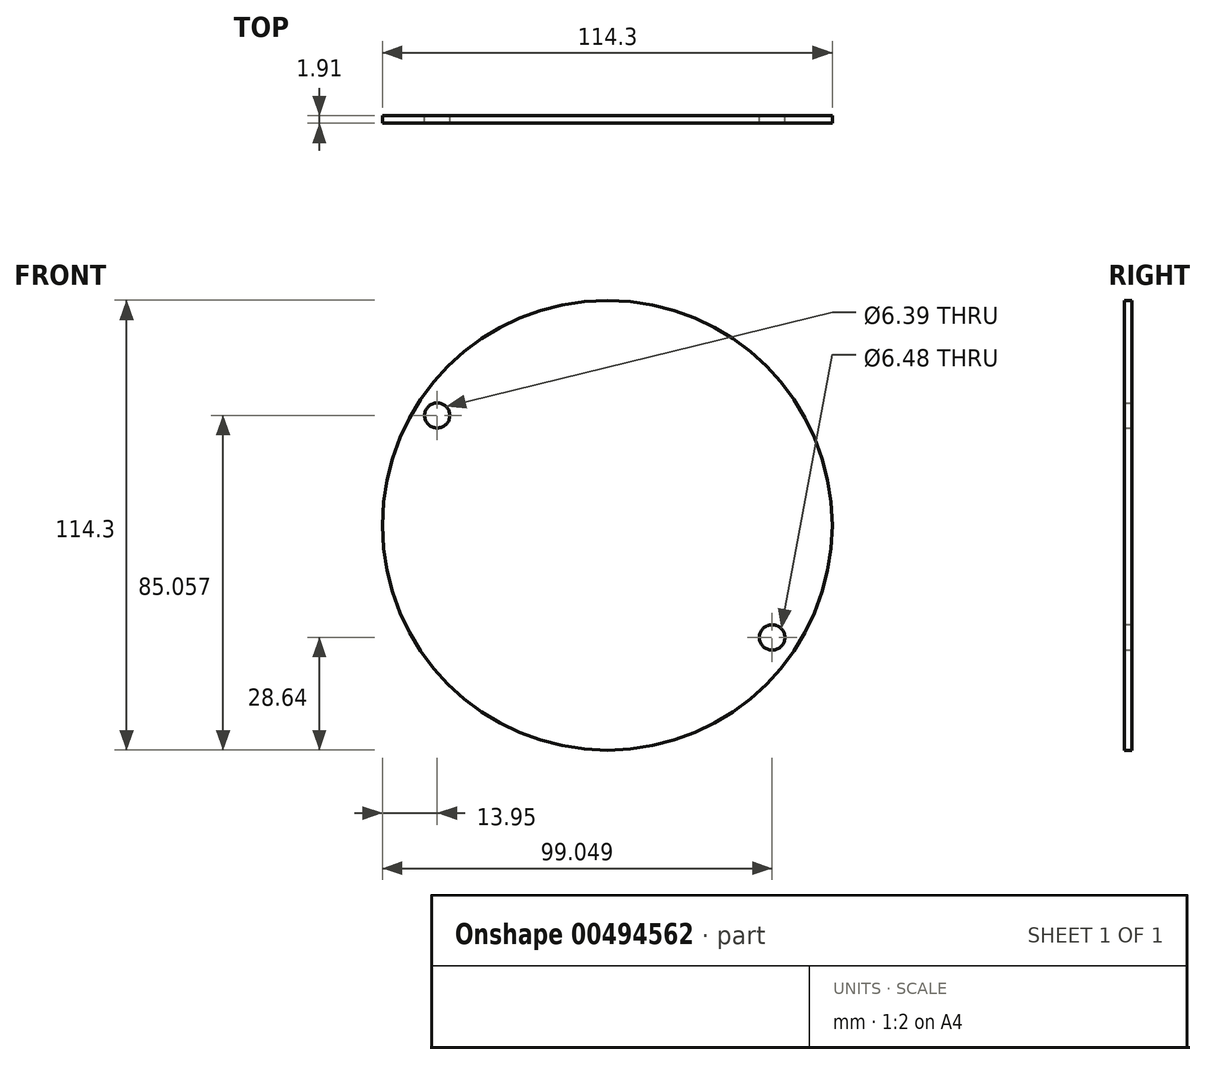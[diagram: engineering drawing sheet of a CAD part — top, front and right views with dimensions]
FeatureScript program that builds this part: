
annotation { "Feature Type Name" : "Feature", "Feature Type Description" : "" }
export const myFeature = defineFeature(function(context is Context, id is Id, definition is map)
    precondition{}
    {
        {
            var Q0;
            Q0=qCreatedBy(makeId("Front.planeOp"),FACE);
            var sketch = newSketch(context, id + "F0", { "sketchPlane" : qUnion([Q0])});
            skCircle(sketch, "E0", {"center": v(-54.97, 31.5) * mm, "radius": 57.15 * mm});
            skCircle(sketch, "E1", {"center": v(-98.17, 59.42) * mm, "radius": 3.2 * mm});
            skCircle(sketch, "E2", {"center": v(-98.17, 59.42) * mm, "radius": 3.18 * mm});
            skCircle(sketch, "E3", {"center": v(-13.07, 3) * mm, "radius": 3.24 * mm});
            skSolve(sketch);
        }
        {
            var Q0;
            Q0 = qSketchRegion(id + "F0", true);
            extrude(context, id + "F1", {"entities" : qUnion([Q0]), "depth" : 1.9 * mm});
        }
    });
